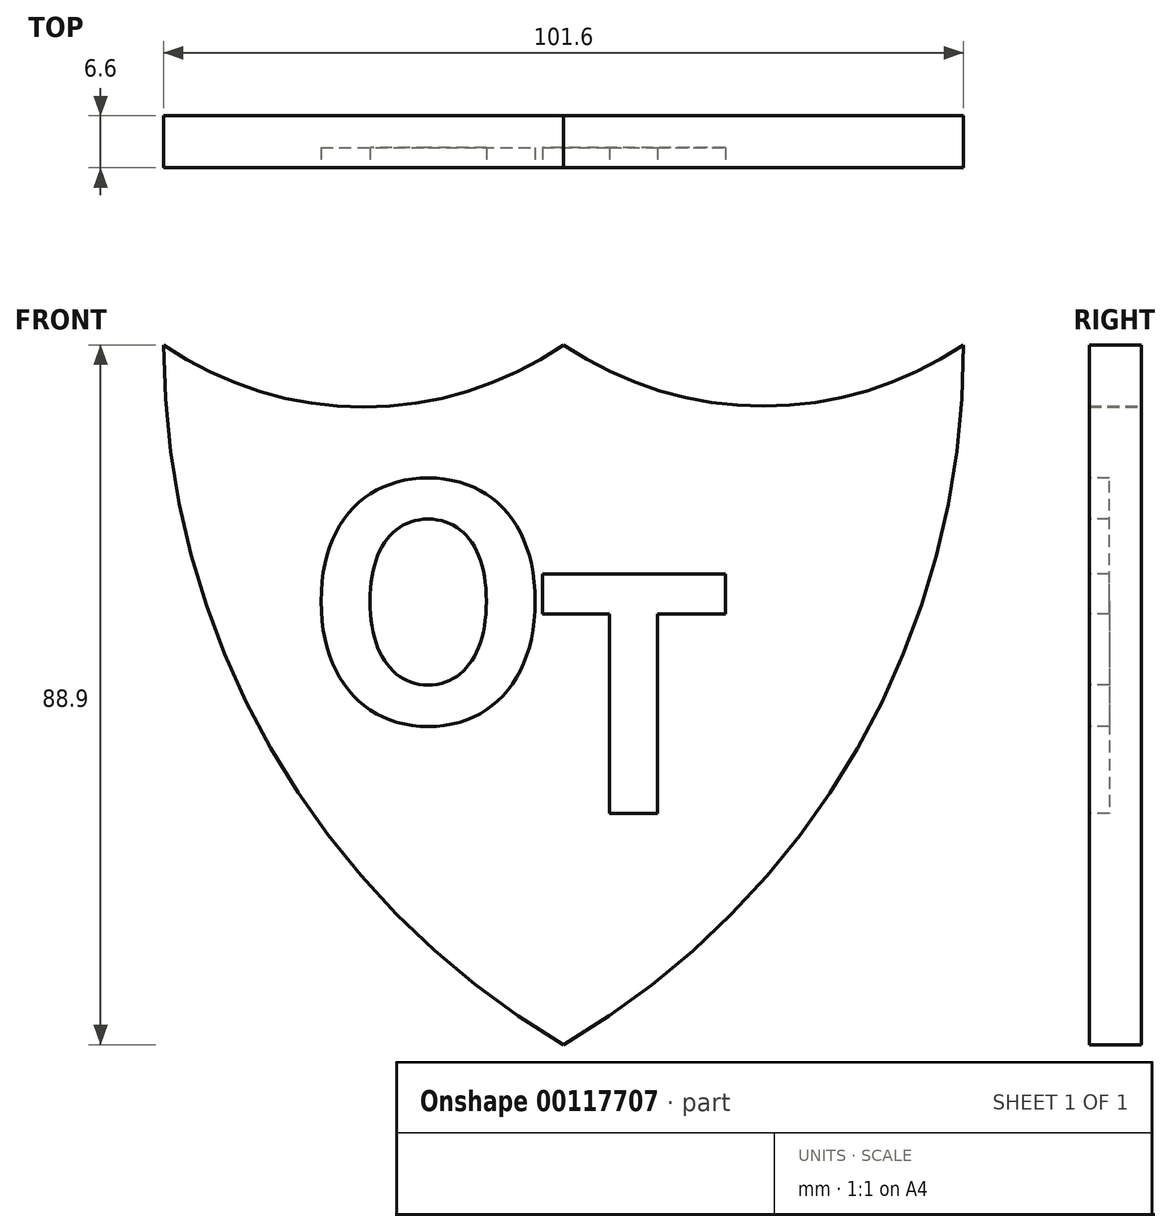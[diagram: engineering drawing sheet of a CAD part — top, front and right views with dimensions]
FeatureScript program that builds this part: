
annotation { "Feature Type Name" : "Feature", "Feature Type Description" : "" }
export const myFeature = defineFeature(function(context is Context, id is Id, definition is map)
    precondition{}
    {
        {
            var Q0;
            Q0=qCreatedBy(makeId("Front.planeOp"),FACE);
            var sketch = newSketch(context, id + "F0", { "sketchPlane" : qUnion([Q0])});
            skArc(sketch, "E0", {"start": v(-50.8, 0) * mm, "mid": v(-37.22, -51.2) * mm, "end": v(0, -88.9) * mm});
            skArc(sketch, "E1", {"start": v(0, -88.9) * mm, "mid": v(37.32, -51.26) * mm, "end": v(50.8, 0) * mm});
            skArc(sketch, "E2", {"start": v(-50.8, 0) * mm, "mid": v(-25.4, -7.9) * mm, "end": v(0, 0) * mm});
            skArc(sketch, "E3", {"start": v(0, 0) * mm, "mid": v(25.4, -7.78) * mm, "end": v(50.8, 0) * mm});
            skSolve(sketch);
        }
        {
            var Q0;
            Q0 = qSketchRegion(id + "F0", true);
            extrude(context, id + "F1", {"entities" : qUnion([Q0]), "depth" : 6.6 * mm});
        }
        {
            var Q0;
            Q0=makeQuery(id+"F1.opExtrude","CAP_FACE",FACE,{"disambiguationData":[OSD([sQuery(id+"F0.wireOp",EDGE,"E0"),sQuery(id+"F0.wireOp",EDGE,"E1"),sQuery(id+"F0.wireOp",EDGE,"E2"),sQuery(id+"F0.wireOp",EDGE,"E3")])],"isStart":false});
            var sketch = newSketch(context, id + "F2", { "sketchPlane" : qUnion([Q0])});
            skText(sketch, "E4", { "text": "O", "fontName": "NotoSansCJKsc-Bold.otf"});
            const initialGuessF2  = {"E4": [-0.03302, -0.0479, 1, 0, 0.02959]};
            skSetInitialGuess(sketch, initialGuessF2);
            skSolve(sketch);
        }
        {
            var Q0;
            Q0 = qSketchRegion(id + "F2", true);
            extrude(context, id + "F3", {"entities" : qUnion([Q0]), "operationType" : NewBodyOperationType.REMOVE, "oppositeDirection" : true, "depth" : 2.54 * mm});
        }
        {
            var Q0;
            {var subQ0=sQuery(id+"F0.wireOp",EDGE,"E3");var subQ1=sQuery(id+"F0.wireOp",EDGE,"E2");var subQ2=sQuery(id+"F0.wireOp",EDGE,"E1");var subQ3=sQuery(id+"F0.wireOp",EDGE,"E0");Q0=makeQuery(id+"F3.boolean.opBoolean","SPLIT",FACE,{"disambiguationData":[TD([makeQuery(id+"F1.opExtrude","SWEPT_FACE",FACE,{"disambiguationData":[OSD([subQ3])]})])],"derivedFrom":makeQuery(id+"F1.opExtrude","CAP_FACE",FACE,{"disambiguationData":[OSD([subQ3,subQ2,subQ1,subQ0])],"isStart":false})});}
            var sketch = newSketch(context, id + "F4", { "sketchPlane" : qUnion([Q0])});
            skText(sketch, "E5", { "text": "T", "fontName": "NotoSansCJKsc-Bold.otf"});
            const initialGuessF4  = {"E5": [-0.00393, -0.05955, 1, 0, 0.0296]};
            skSetInitialGuess(sketch, initialGuessF4);
            skSolve(sketch);
        }
        {
            var Q0;
            Q0 = qSketchRegion(id + "F4", true);
            extrude(context, id + "F5", {"entities" : qUnion([Q0]), "operationType" : NewBodyOperationType.REMOVE, "oppositeDirection" : true, "depth" : 2.54 * mm});
        }
    });
